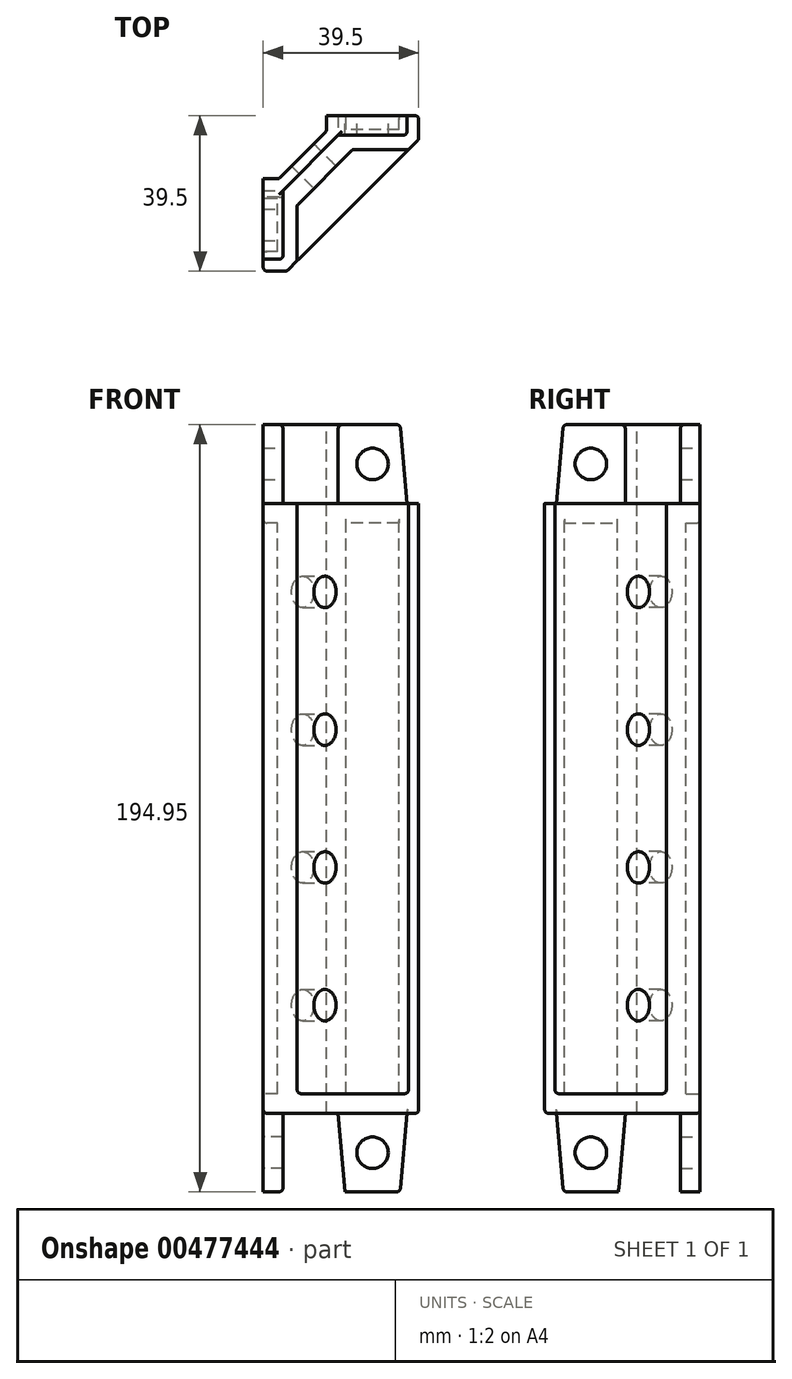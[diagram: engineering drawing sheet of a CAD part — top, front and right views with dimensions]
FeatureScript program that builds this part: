
annotation { "Feature Type Name" : "Feature", "Feature Type Description" : "" }
export const myFeature = defineFeature(function(context is Context, id is Id, definition is map)
    precondition{}
    {
        {
            var Q0;
            Q0=qCreatedBy(makeId("Top.planeOp"),FACE);
            var sketch = newSketch(context, id + "F0", { "sketchPlane" : qUnion([Q0])});
            skLineSegment(sketch, "E0", {"start": v(0, 30.13) * mm, "end": v(0, -27.95) * mm, "construction": true});
            skLineSegment(sketch, "E1", {"start": v(-25.65, 0) * mm, "end": v(27.57, 0) * mm, "construction": true});
            skLineSegment(sketch, "E2.bottom", {"start": v(-19.75, 19.75) * mm, "end": v(19.75, 19.75) * mm});
            skLineSegment(sketch, "E2.top", {"start": v(-19.75, -19.75) * mm, "end": v(-13.75, -19.75) * mm});
            skLineSegment(sketch, "E2.left", {"start": v(-19.75, 19.75) * mm, "end": v(-19.75, -19.75) * mm});
            skLineSegment(sketch, "E2.right", {"start": v(19.75, 19.75) * mm, "end": v(19.75, 13.75) * mm});
            skLineSegment(sketch, "E3", {"start": v(-13.75, -19.75) * mm, "end": v(19.75, 13.75) * mm});
            skSolve(sketch);
        }
        {
            var Q0;
            Q0 = qSketchRegion(id + "F0", true);
            extrude(context, id + "F1", {"entities" : qUnion([Q0]), "oppositeDirection" : true, "depth" : 155 * mm, "symmetric" : true});
        }
        {
            var Q0;
            Q0=makeQuery(id+"F1.opExtrude","CAP_FACE",FACE,{"disambiguationData":[OSD([sQuery(id+"F0.wireOp",EDGE,"E2.bottom"),sQuery(id+"F0.wireOp",EDGE,"E2.top"),sQuery(id+"F0.wireOp",EDGE,"E2.left"),sQuery(id+"F0.wireOp",EDGE,"E2.right"),sQuery(id+"F0.wireOp",EDGE,"E3")])],"isStart":true});
            var sketch = newSketch(context, id + "F2", { "sketchPlane" : qUnion([Q0])});
            skLineSegment(sketch, "E4", {"start": v(3, -3) * mm, "end": v(-19.75, 19.75) * mm, "construction": true});
            skLineSegment(sketch, "E5", {"start": v(3, -3) * mm, "end": v(17.14, 11.14) * mm});
            skLineSegment(sketch, "E6", {"start": v(3, -3) * mm, "end": v(-11.14, -17.14) * mm});
            skLineSegment(sketch, "E7", {"start": v(-11.14, -3) * mm, "end": v(3, 11.14) * mm});
            skLineSegment(sketch, "E8", {"start": v(-11.14, -17.14) * mm, "end": v(-11.14, -3) * mm});
            skLineSegment(sketch, "E9", {"start": v(3, 11.14) * mm, "end": v(17.14, 11.14) * mm});
            skSolve(sketch);
        }
        {
            var Q0;
            Q0 = qSketchRegion(id + "F2", true);
            extrude(context, id + "F3", {"entities" : qUnion([Q0]), "operationType" : NewBodyOperationType.REMOVE, "oppositeDirection" : true, "depth" : 150 * mm});
        }
        {
            var Q0;
            Q0=makeQuery(id+"F1.opExtrude","CAP_FACE",FACE,{"disambiguationData":[OSD([sQuery(id+"F0.wireOp",EDGE,"E2.bottom"),sQuery(id+"F0.wireOp",EDGE,"E2.top"),sQuery(id+"F0.wireOp",EDGE,"E2.left"),sQuery(id+"F0.wireOp",EDGE,"E2.right"),sQuery(id+"F0.wireOp",EDGE,"E3")])],"isStart":true});
            var sketch = newSketch(context, id + "F4", { "sketchPlane" : qUnion([Q0])});
            skPoint(sketch, "E10.orphan", {"position": v(-19.75, -19.75) * mm});
            skPoint(sketch, "E11.orphan", {"position": v(19.75, 19.75) * mm});
            skLineSegment(sketch, "E12", {"start": v(-19.75, 19.75) * mm, "end": v(-4.07, 4.07) * mm, "construction": true});
            skLineSegment(sketch, "E13", {"start": v(-15.75, 3.7) * mm, "end": v(-19.75, 3.7) * mm});
            skLineSegment(sketch, "E14", {"start": v(-3.7, 15.75) * mm, "end": v(-3.7, 19.75) * mm});
            skLineSegment(sketch, "E15", {"start": v(-3.7, 19.75) * mm, "end": v(-19.75, 19.75) * mm});
            skLineSegment(sketch, "E16", {"start": v(-19.75, 19.75) * mm, "end": v(-19.75, 3.7) * mm});
            skLineSegment(sketch, "E17", {"start": v(-3.7, 15.75) * mm, "end": v(-15.75, 3.7) * mm});
            skPoint(sketch, "E18.orphan", {"position": v(-14.68, 3.7) * mm});
            skPoint(sketch, "E19.orphan", {"position": v(-3.7, 13.6) * mm});
            skSolve(sketch);
        }
        {
            var Q0;
            Q0 = qSketchRegion(id + "F4", true);
            extrude(context, id + "F5", {"entities" : qUnion([Q0]), "operationType" : NewBodyOperationType.REMOVE, "endBound" : BoundingType.THROUGH_ALL, "oppositeDirection" : true, "depth" : 25 * mm});
        }
        {
            var Q0;
            Q0=makeQuery(id+"F1.opExtrude","CAP_FACE",FACE,{"disambiguationData":[OSD([sQuery(id+"F0.wireOp",EDGE,"E2.bottom"),sQuery(id+"F0.wireOp",EDGE,"E2.top"),sQuery(id+"F0.wireOp",EDGE,"E2.left"),sQuery(id+"F0.wireOp",EDGE,"E2.right"),sQuery(id+"F0.wireOp",EDGE,"E3")])],"isStart":true});
            var sketch = newSketch(context, id + "F6", { "sketchPlane" : qUnion([Q0])});
            skLineSegment(sketch, "E20.0", {"start": v(1.3, 16.14) * mm, "end": v(14.75, 16.14) * mm});
            skLineSegment(sketch, "E20.1", {"start": v(14.75, 19.75) * mm, "end": v(14.75, 16.14) * mm});
            skLineSegment(sketch, "E21.0", {"start": v(1.3, 16.14) * mm, "end": v(1.3, 19.75) * mm});
            skLineSegment(sketch, "E22", {"start": v(14.75, 19.75) * mm, "end": v(1.3, 19.75) * mm});
            skLineSegment(sketch, "E23.0", {"start": v(-16.14, -14.75) * mm, "end": v(-16.14, -1.3) * mm});
            skLineSegment(sketch, "E23.1", {"start": v(-19.75, -14.75) * mm, "end": v(-16.14, -14.75) * mm});
            skLineSegment(sketch, "E24.0", {"start": v(-16.14, -1.3) * mm, "end": v(-19.75, -1.3) * mm});
            skPoint(sketch, "E25.orphan", {"position": v(-12.53, -1.3) * mm});
            skLineSegment(sketch, "E26", {"start": v(-19.75, -14.75) * mm, "end": v(-19.75, -1.3) * mm});
            skSolve(sketch);
        }
        {
            var Q0;
            Q0 = qSketchRegion(id + "F6", true);
            extrude(context, id + "F7", {"entities" : qUnion([Q0]), "operationType" : NewBodyOperationType.REMOVE, "endBound" : BoundingType.THROUGH_ALL, "oppositeDirection" : true, "depth" : 25 * mm});
        }
        {
            var Q0;
            {var subQ1=sQuery(id+"F0.wireOp",EDGE,"E2.right");var subQ4=sQuery(id+"F0.wireOp",EDGE,"E2.bottom");Q0=makeQuery(id+"F7.boolean.opBoolean","SPLIT",FACE,{"disambiguationData":[TD([makeQuery(id+"F1.opExtrude","SWEPT_FACE",FACE,{"disambiguationData":[OSD([subQ1])]})])],"derivedFrom":makeQuery(id+"F1.opExtrude","SWEPT_FACE",FACE,{"disambiguationData":[OSD([subQ4])]})});}
            var sketch = newSketch(context, id + "F8", { "sketchPlane" : qUnion([Q0])});
            skLineSegment(sketch, "E27.bottom", {"start": v(-14.75, 77.5) * mm, "end": v(-1.3, 77.5) * mm});
            skLineSegment(sketch, "E27.top", {"start": v(-14.75, 72.5) * mm, "end": v(-1.3, 72.5) * mm});
            skLineSegment(sketch, "E27.left", {"start": v(-14.75, 77.5) * mm, "end": v(-14.75, 72.5) * mm});
            skLineSegment(sketch, "E27.right", {"start": v(-1.3, 77.5) * mm, "end": v(-1.3, 72.5) * mm});
            skLineSegment(sketch, "E28.bottom", {"start": v(-14.75, -77.5) * mm, "end": v(-1.3, -77.5) * mm});
            skLineSegment(sketch, "E28.top", {"start": v(-14.75, -72.5) * mm, "end": v(-1.3, -72.5) * mm});
            skLineSegment(sketch, "E28.left", {"start": v(-14.75, -77.5) * mm, "end": v(-14.75, -72.5) * mm});
            skLineSegment(sketch, "E28.right", {"start": v(-1.3, -77.5) * mm, "end": v(-1.3, -72.5) * mm});
            skSolve(sketch);
        }
        {
            var Q0;
            Q0 = qSketchRegion(id + "F8", true);
            var Q1;
            Q1=makeQuery(id+"F7.boolean.opBoolean","COPY",FACE,{"derivedFrom":makeQuery(id+"F7.opExtrude","SWEPT_FACE",FACE,{"disambiguationData":[OSD([sQuery(id+"F6.wireOp",EDGE,"E20.0")])]})});
            extrude(context, id + "F9", {"entities" : qUnion([Q0]), "operationType" : NewBodyOperationType.ADD, "endBound" : BoundingType.UP_TO_SURFACE, "oppositeDirection" : true, "endBoundEntityFace" : qUnion([Q1]), "depth" : 25 * mm});
        }
        {
            var Q0;
            {var subQ2=sQuery(id+"F0.wireOp",EDGE,"E2.left");var subQ3=sQuery(id+"F0.wireOp",EDGE,"E2.top");Q0=makeQuery(id+"F7.boolean.opBoolean","SPLIT",FACE,{"disambiguationData":[TD([makeQuery(id+"F1.opExtrude","SWEPT_FACE",FACE,{"disambiguationData":[OSD([subQ3])]})])],"derivedFrom":makeQuery(id+"F1.opExtrude","SWEPT_FACE",FACE,{"disambiguationData":[OSD([subQ2])]})});}
            var sketch = newSketch(context, id + "F10", { "sketchPlane" : qUnion([Q0])});
            skLineSegment(sketch, "E29.bottom", {"start": v(14.75, 77.5) * mm, "end": v(1.3, 77.5) * mm});
            skLineSegment(sketch, "E29.top", {"start": v(14.75, 72.5) * mm, "end": v(1.3, 72.5) * mm});
            skLineSegment(sketch, "E29.left", {"start": v(14.75, 77.5) * mm, "end": v(14.75, 72.5) * mm});
            skLineSegment(sketch, "E29.right", {"start": v(1.3, 77.5) * mm, "end": v(1.3, 72.5) * mm});
            skLineSegment(sketch, "E30.bottom", {"start": v(14.75, -77.5) * mm, "end": v(1.3, -77.5) * mm});
            skLineSegment(sketch, "E30.top", {"start": v(14.75, -72.5) * mm, "end": v(1.3, -72.5) * mm});
            skLineSegment(sketch, "E30.left", {"start": v(14.75, -77.5) * mm, "end": v(14.75, -72.5) * mm});
            skLineSegment(sketch, "E30.right", {"start": v(1.3, -77.5) * mm, "end": v(1.3, -72.5) * mm});
            skSolve(sketch);
        }
        {
            var Q0;
            Q0 = qSketchRegion(id + "F10", true);
            var Q1;
            Q1=makeQuery(id+"F7.boolean.opBoolean","COPY",FACE,{"derivedFrom":makeQuery(id+"F7.opExtrude","SWEPT_FACE",FACE,{"disambiguationData":[OSD([sQuery(id+"F6.wireOp",EDGE,"E23.0")])]})});
            extrude(context, id + "F11", {"entities" : qUnion([Q0]), "operationType" : NewBodyOperationType.ADD, "endBound" : BoundingType.UP_TO_SURFACE, "oppositeDirection" : true, "endBoundEntityFace" : qUnion([Q1]), "depth" : 25 * mm});
        }
        {
            var Q0;
            {var subQ2=sQuery(id+"F0.wireOp",EDGE,"E2.left");var subQ3=sQuery(id+"F0.wireOp",EDGE,"E2.top");var subQ7=makeQuery(id+"F1.opExtrude","SWEPT_FACE",FACE,{"disambiguationData":[OSD([subQ2])]});Q0=makeQuery(id+"F11.boolean.opBoolean","MERGE",FACE,{"derivedFrom":[makeQuery(id+"F7.boolean.opBoolean","SPLIT",FACE,{"disambiguationData":[TD([makeQuery(id+"F1.opExtrude","SWEPT_FACE",FACE,{"disambiguationData":[OSD([subQ3])]})])],"derivedFrom":subQ7}),makeQuery(id+"F7.boolean.opBoolean","SPLIT",FACE,{"disambiguationData":[TD([makeQuery(id+"F5.boolean.opBoolean","COPY",FACE,{"derivedFrom":makeQuery(id+"F5.opExtrude","SWEPT_FACE",FACE,{"disambiguationData":[OSD([sQuery(id+"F4.wireOp",EDGE,"E13")])]})})])],"derivedFrom":subQ7}),makeQuery(id+"F11.opExtrude","CAP_FACE",FACE,{"disambiguationData":[OSD([sQuery(id+"F10.wireOp",EDGE,"E29.bottom"),sQuery(id+"F10.wireOp",EDGE,"E29.top"),sQuery(id+"F10.wireOp",EDGE,"E29.left"),sQuery(id+"F10.wireOp",EDGE,"E29.right")])],"isStart":true}),makeQuery(id+"F11.opExtrude","CAP_FACE",FACE,{"disambiguationData":[OSD([sQuery(id+"F10.wireOp",EDGE,"E30.bottom"),sQuery(id+"F10.wireOp",EDGE,"E30.top"),sQuery(id+"F10.wireOp",EDGE,"E30.left"),sQuery(id+"F10.wireOp",EDGE,"E30.right")])],"isStart":true})]});}
            var sketch = newSketch(context, id + "F12", { "sketchPlane" : qUnion([Q0])});
            skLineSegment(sketch, "E31", {"start": v(8.02, 77.5) * mm, "end": v(8.02, 97.5) * mm, "construction": true});
            skLineSegment(sketch, "E32", {"start": v(0, 0) * mm, "end": v(35.4, 0) * mm, "construction": true});
            skPoint(sketch, "E32.endSnap0", {"position": v(19.75, 0) * mm});
            skLineSegment(sketch, "E33.MirrorCS", {"start": v(16.04, 0) * mm, "end": v(-19.35, 0) * mm, "construction": true});
            skLineSegment(sketch, "E34", {"start": v(16.75, 77.5) * mm, "end": v(-0.7, 77.5) * mm});
            skLineSegment(sketch, "E35", {"start": v(16.75, 77.5) * mm, "end": v(15.02, 97.5) * mm});
            skLineSegment(sketch, "E36", {"start": v(15.02, 97.5) * mm, "end": v(8.02, 97.5) * mm});
            skLineSegment(sketch, "E37", {"start": v(8.02, 97.5) * mm, "end": v(1.02, 97.5) * mm});
            skLineSegment(sketch, "E38", {"start": v(1.02, 97.5) * mm, "end": v(-0.7, 77.5) * mm});
            skLineSegment(sketch, "E39.MirrorCS", {"start": v(-0.7, 77.5) * mm, "end": v(1.02, 97.5) * mm});
            skSolve(sketch);
        }
        {
            var Q0;
            Q0 = qSketchRegion(id + "F12", true);
            extrude(context, id + "F13", {"entities" : qUnion([Q0]), "operationType" : NewBodyOperationType.ADD, "oppositeDirection" : true, "depth" : 5 * mm});
        }
        {
            var Q0;
            {var subQ1=sQuery(id+"F0.wireOp",EDGE,"E2.right");var subQ4=sQuery(id+"F0.wireOp",EDGE,"E2.bottom");var subQ7=makeQuery(id+"F1.opExtrude","SWEPT_FACE",FACE,{"disambiguationData":[OSD([subQ4])]});Q0=makeQuery(id+"F9.boolean.opBoolean","MERGE",FACE,{"derivedFrom":[makeQuery(id+"F7.boolean.opBoolean","SPLIT",FACE,{"disambiguationData":[TD([makeQuery(id+"F1.opExtrude","SWEPT_FACE",FACE,{"disambiguationData":[OSD([subQ1])]})])],"derivedFrom":subQ7}),makeQuery(id+"F7.boolean.opBoolean","SPLIT",FACE,{"disambiguationData":[TD([makeQuery(id+"F5.boolean.opBoolean","COPY",FACE,{"derivedFrom":makeQuery(id+"F5.opExtrude","SWEPT_FACE",FACE,{"disambiguationData":[OSD([sQuery(id+"F4.wireOp",EDGE,"E14")])]})})])],"derivedFrom":subQ7}),makeQuery(id+"F9.opExtrude","CAP_FACE",FACE,{"disambiguationData":[OSD([sQuery(id+"F8.wireOp",EDGE,"E27.bottom"),sQuery(id+"F8.wireOp",EDGE,"E27.top"),sQuery(id+"F8.wireOp",EDGE,"E27.left"),sQuery(id+"F8.wireOp",EDGE,"E27.right")])],"isStart":true}),makeQuery(id+"F9.opExtrude","CAP_FACE",FACE,{"disambiguationData":[OSD([sQuery(id+"F8.wireOp",EDGE,"E28.bottom"),sQuery(id+"F8.wireOp",EDGE,"E28.top"),sQuery(id+"F8.wireOp",EDGE,"E28.left"),sQuery(id+"F8.wireOp",EDGE,"E28.right")])],"isStart":true})]});}
            var sketch = newSketch(context, id + "F14", { "sketchPlane" : qUnion([Q0])});
            skLineSegment(sketch, "E40", {"start": v(-8.02, 77.5) * mm, "end": v(-8.02, 97.66) * mm, "construction": true});
            skPoint(sketch, "E40.endSnap0", {"position": v(-8.02, 77.5) * mm});
            skLineSegment(sketch, "E41", {"start": v(-15.02, 97.5) * mm, "end": v(-1.02, 97.5) * mm});
            skLineSegment(sketch, "E42", {"start": v(0, 0) * mm, "end": v(-60.6, 0) * mm, "construction": true});
            skPoint(sketch, "E42.endSnap0", {"position": v(-14.75, 0) * mm});
            skLineSegment(sketch, "E43", {"start": v(-15.02, 97.5) * mm, "end": v(-16.75, 77.5) * mm});
            skLineSegment(sketch, "E44", {"start": v(-1.02, 97.5) * mm, "end": v(0.7, 77.5) * mm});
            skLineSegment(sketch, "E45", {"start": v(0.7, 77.5) * mm, "end": v(-16.75, 77.5) * mm});
            skSolve(sketch);
        }
        {
            var Q0;
            Q0 = qSketchRegion(id + "F14", true);
            extrude(context, id + "F15", {"entities" : qUnion([Q0]), "operationType" : NewBodyOperationType.ADD, "oppositeDirection" : true, "depth" : 5 * mm});
        }
        {
            var Q0;
            {var subQ1=sQuery(id+"F0.wireOp",EDGE,"E2.right");var subQ4=sQuery(id+"F0.wireOp",EDGE,"E2.bottom");var subQ7=makeQuery(id+"F1.opExtrude","SWEPT_FACE",FACE,{"disambiguationData":[OSD([subQ4])]});Q0=makeQuery(id+"F15.boolean.opBoolean","MERGE",FACE,{"derivedFrom":[makeQuery(id+"F9.boolean.opBoolean","MERGE",FACE,{"derivedFrom":[makeQuery(id+"F7.boolean.opBoolean","SPLIT",FACE,{"disambiguationData":[TD([makeQuery(id+"F1.opExtrude","SWEPT_FACE",FACE,{"disambiguationData":[OSD([subQ1])]})])],"derivedFrom":subQ7}),makeQuery(id+"F7.boolean.opBoolean","SPLIT",FACE,{"disambiguationData":[TD([makeQuery(id+"F5.boolean.opBoolean","COPY",FACE,{"derivedFrom":makeQuery(id+"F5.opExtrude","SWEPT_FACE",FACE,{"disambiguationData":[OSD([sQuery(id+"F4.wireOp",EDGE,"E14")])]})})])],"derivedFrom":subQ7}),makeQuery(id+"F9.opExtrude","CAP_FACE",FACE,{"disambiguationData":[OSD([sQuery(id+"F8.wireOp",EDGE,"E27.bottom"),sQuery(id+"F8.wireOp",EDGE,"E27.top"),sQuery(id+"F8.wireOp",EDGE,"E27.left"),sQuery(id+"F8.wireOp",EDGE,"E27.right")])],"isStart":true}),makeQuery(id+"F9.opExtrude","CAP_FACE",FACE,{"disambiguationData":[OSD([sQuery(id+"F8.wireOp",EDGE,"E28.bottom"),sQuery(id+"F8.wireOp",EDGE,"E28.top"),sQuery(id+"F8.wireOp",EDGE,"E28.left"),sQuery(id+"F8.wireOp",EDGE,"E28.right")])],"isStart":true})]}),makeQuery(id+"F15.opExtrude","CAP_FACE",FACE,{"disambiguationData":[OSD([sQuery(id+"F14.wireOp",EDGE,"AjdLOBUI-PND2-HRux-vW9i-I60BuJFxOAxo"),sQuery(id+"F14.wireOp",EDGE,"m2E0O1S7-ugW4-w8lP-xUBK-8UGrL3XVD3p1"),sQuery(id+"F14.wireOp",EDGE,"E41"),sQuery(id+"F14.wireOp",EDGE,"z751VbyZ-Eswl-sp4i-D6d8-2ebrKqnJ25gN")])],"isStart":true}),makeQuery(id+"F15.opExtrude","CAP_FACE",FACE,{"disambiguationData":[OSD([sQuery(id+"F14.wireOp",EDGE,"9fced805-f766-4b14-a849-f1590210c0c81.MirrorCS"),sQuery(id+"F14.wireOp",EDGE,"9fced805-f766-4b14-a849-f1590210c0c82.MirrorCS"),sQuery(id+"F14.wireOp",EDGE,"9fced805-f766-4b14-a849-f1590210c0c83.MirrorCS"),sQuery(id+"F14.wireOp",EDGE,"9fced805-f766-4b14-a849-f1590210c0c84.MirrorCS")])],"isStart":true})]});}
            var sketch = newSketch(context, id + "F16", { "sketchPlane" : qUnion([Q0])});
            skLineSegment(sketch, "E46", {"start": v(-8.02, 97.5) * mm, "end": v(-8.02, -141.14) * mm, "construction": true});
            skCircle(sketch, "E47", {"center": v(-8.02, 87.5) * mm, "radius": 4 * mm});
            skSolve(sketch);
        }
        {
            var Q0;
            Q0 = qSketchRegion(id + "F16", true);
            extrude(context, id + "F17", {"entities" : qUnion([Q0]), "operationType" : NewBodyOperationType.REMOVE, "endBound" : BoundingType.THROUGH_ALL, "oppositeDirection" : true, "depth" : 25 * mm});
        }
        {
            var Q0;
            Q0=makeQuery(id+"F3.boolean.opBoolean","COPY",FACE,{"derivedFrom":makeQuery(id+"F3.opExtrude","SWEPT_FACE",FACE,{"disambiguationData":[OSD([sQuery(id+"F2.wireOp",EDGE,"E7")])]})});
            var sketch = newSketch(context, id + "F18", { "sketchPlane" : qUnion([Q0])});
            skLineSegment(sketch, "E48", {"start": v(0, 77.5) * mm, "end": v(0, -72.5) * mm, "construction": true});
            skLineSegment(sketch, "E49", {"start": v(0, 2.5) * mm, "end": v(10, 2.5) * mm, "construction": true});
            skCircle(sketch, "E50", {"center": v(0, 55) * mm, "radius": 4 * mm});
            skCircle(sketch, "E51", {"center": v(0, 20) * mm, "radius": 4 * mm});
            skCircle(sketch, "E52.MirrorC", {"center": v(0, -50) * mm, "radius": 4 * mm});
            skCircle(sketch, "E53.MirrorC", {"center": v(0, -15) * mm, "radius": 4 * mm});
            skSolve(sketch);
        }
        {
            var Q0;
            Q0 = qSketchRegion(id + "F18", true);
            extrude(context, id + "F19", {"entities" : qUnion([Q0]), "operationType" : NewBodyOperationType.REMOVE, "endBound" : BoundingType.THROUGH_ALL, "oppositeDirection" : true, "depth" : 25 * mm});
        }
        {
            var Q0;
            Q0=makeQuery(id+"F13.opExtrude","CAP_FACE",FACE,{"disambiguationData":[OSD([sQuery(id+"F12.wireOp",EDGE,"E34"),sQuery(id+"F12.wireOp",EDGE,"E35"),sQuery(id+"F12.wireOp",EDGE,"E36"),sQuery(id+"F12.wireOp",EDGE,"E37"),sQuery(id+"F12.wireOp",EDGE,"E39.MirrorCS")])],"isStart":false});
            var sketch = newSketch(context, id + "F20", { "sketchPlane" : qUnion([Q0])});
            skLineSegment(sketch, "E54", {"start": v(-8.02, 97.5) * mm, "end": v(-8.02, -97.5) * mm, "construction": true});
            skPoint(sketch, "E54.endSnap0", {"position": v(-8.02, 97.5) * mm});
            skCircle(sketch, "E55", {"center": v(-8.02, 87.5) * mm, "radius": 4 * mm});
            skSolve(sketch);
        }
        {
            var Q0;
            Q0 = qSketchRegion(id + "F20", true);
            extrude(context, id + "F21", {"entities" : qUnion([Q0]), "operationType" : NewBodyOperationType.REMOVE, "endBound" : BoundingType.THROUGH_ALL, "oppositeDirection" : true, "depth" : 25 * mm});
        }
        {
            var Q0;
            Q0=makeQuery(id+"F13.opExtrude","CAP_FACE",FACE,{"disambiguationData":[OSD([sQuery(id+"F12.wireOp",EDGE,"E34"),sQuery(id+"F12.wireOp",EDGE,"E35"),sQuery(id+"F12.wireOp",EDGE,"E36"),sQuery(id+"F12.wireOp",EDGE,"E37"),sQuery(id+"F12.wireOp",EDGE,"E39.MirrorCS")])],"isStart":false});
            var sketch = newSketch(context, id + "F22", { "sketchPlane" : qUnion([Q0])});
            skLineSegment(sketch, "E56", {"start": v(-16.75, -77.5) * mm, "end": v(-15.02, -97.5) * mm});
            skLineSegment(sketch, "E57", {"start": v(-15.02, -97.5) * mm, "end": v(-8.02, -97.5) * mm});
            skLineSegment(sketch, "E58", {"start": v(-8.02, -97.5) * mm, "end": v(-8.02, 83.5) * mm, "construction": true});
            skLineSegment(sketch, "E59.MirrorCS", {"start": v(0.7, -77.5) * mm, "end": v(-1.02, -97.5) * mm});
            skLineSegment(sketch, "E60.MirrorCS", {"start": v(-1.02, -97.5) * mm, "end": v(-8.02, -97.5) * mm});
            skLineSegment(sketch, "E61", {"start": v(-16.75, -77.5) * mm, "end": v(0.7, -77.5) * mm});
            skSolve(sketch);
        }
        {
            var Q0;
            Q0 = qSketchRegion(id + "F22", true);
            extrude(context, id + "F23", {"entities" : qUnion([Q0]), "operationType" : NewBodyOperationType.ADD, "oppositeDirection" : true, "depth" : 5 * mm});
        }
        {
            var Q0;
            Q0=makeQuery(id+"F15.opExtrude","CAP_FACE",FACE,{"disambiguationData":[OSD([sQuery(id+"F14.wireOp",EDGE,"E41"),sQuery(id+"F14.wireOp",EDGE,"E43"),sQuery(id+"F14.wireOp",EDGE,"E44"),sQuery(id+"F14.wireOp",EDGE,"E45")])],"isStart":false});
            var sketch = newSketch(context, id + "F24", { "sketchPlane" : qUnion([Q0])});
            skLineSegment(sketch, "E62", {"start": v(-0.7, -77.5) * mm, "end": v(1.02, -97.5) * mm});
            skLineSegment(sketch, "E63", {"start": v(1.02, -97.5) * mm, "end": v(8.02, -97.5) * mm});
            skLineSegment(sketch, "E64", {"start": v(8.02, -97.5) * mm, "end": v(8.02, -77.04) * mm, "construction": true});
            skLineSegment(sketch, "E65.MirrorCS", {"start": v(16.75, -77.5) * mm, "end": v(15.02, -97.5) * mm});
            skLineSegment(sketch, "E66.MirrorCS", {"start": v(15.02, -97.5) * mm, "end": v(8.02, -97.5) * mm});
            skLineSegment(sketch, "E67", {"start": v(-0.7, -77.5) * mm, "end": v(16.75, -77.5) * mm});
            skSolve(sketch);
        }
        {
            var Q0;
            Q0 = qSketchRegion(id + "F24", true);
            extrude(context, id + "F25", {"entities" : qUnion([Q0]), "operationType" : NewBodyOperationType.ADD, "oppositeDirection" : true, "depth" : 5 * mm});
        }
        {
            var Q0;
            Q0=makeQuery(id+"F23.opExtrude","CAP_FACE",FACE,{"disambiguationData":[OSD([sQuery(id+"F22.wireOp",EDGE,"E56"),sQuery(id+"F22.wireOp",EDGE,"E57"),sQuery(id+"F22.wireOp",EDGE,"E59.MirrorCS"),sQuery(id+"F22.wireOp",EDGE,"E60.MirrorCS"),sQuery(id+"F22.wireOp",EDGE,"E61")])],"isStart":false});
            var sketch = newSketch(context, id + "F26", { "sketchPlane" : qUnion([Q0])});
            skLineSegment(sketch, "E68", {"start": v(8.02, -97.5) * mm, "end": v(8.02, -77.5) * mm, "construction": true});
            skCircle(sketch, "E69", {"center": v(8.02, -87.5) * mm, "radius": 4 * mm});
            skSolve(sketch);
        }
        {
            var Q0;
            Q0 = qSketchRegion(id + "F26", true);
            extrude(context, id + "F27", {"entities" : qUnion([Q0]), "operationType" : NewBodyOperationType.REMOVE, "oppositeDirection" : true, "depth" : 25 * mm});
        }
        {
            var Q0;
            Q0=makeQuery(id+"F25.opExtrude","CAP_FACE",FACE,{"disambiguationData":[OSD([sQuery(id+"F24.wireOp",EDGE,"E62"),sQuery(id+"F24.wireOp",EDGE,"E63"),sQuery(id+"F24.wireOp",EDGE,"E65.MirrorCS"),sQuery(id+"F24.wireOp",EDGE,"E66.MirrorCS"),sQuery(id+"F24.wireOp",EDGE,"E67")])],"isStart":false});
            var sketch = newSketch(context, id + "F28", { "sketchPlane" : qUnion([Q0])});
            skLineSegment(sketch, "E70", {"start": v(-8.02, -97.5) * mm, "end": v(-8.02, -77.5) * mm, "construction": true});
            skCircle(sketch, "E71", {"center": v(-8.02, -87.5) * mm, "radius": 4 * mm});
            skSolve(sketch);
        }
        {
            var Q0;
            Q0 = qSketchRegion(id + "F28", true);
            extrude(context, id + "F29", {"entities" : qUnion([Q0]), "operationType" : NewBodyOperationType.REMOVE, "oppositeDirection" : true, "depth" : 25 * mm});
        }
        {
            var Q0;
            Q0=makeQuery(id+"F11.boolean.opBoolean","MERGE",FACE,{"derivedFrom":[makeQuery(id+"F9.boolean.opBoolean","MERGE",FACE,{"derivedFrom":[makeQuery(id+"F1.opExtrude","CAP_FACE",FACE,{"disambiguationData":[OSD([sQuery(id+"F0.wireOp",EDGE,"E2.bottom"),sQuery(id+"F0.wireOp",EDGE,"E2.top"),sQuery(id+"F0.wireOp",EDGE,"E2.left"),sQuery(id+"F0.wireOp",EDGE,"E2.right"),sQuery(id+"F0.wireOp",EDGE,"E3")])],"isStart":true}),makeQuery(id+"F9.opExtrude","SWEPT_FACE",FACE,{"disambiguationData":[OSD([sQuery(id+"F8.wireOp",EDGE,"E27.bottom")])]})]}),makeQuery(id+"F11.opExtrude","SWEPT_FACE",FACE,{"disambiguationData":[OSD([sQuery(id+"F10.wireOp",EDGE,"E29.bottom")])]})]});
            var sketch = newSketch(context, id + "F30", { "sketchPlane" : qUnion([Q0])});
            skLineSegment(sketch, "E72.0", {"start": v(-19.75, 0.7) * mm, "end": v(-19.75, -1.02) * mm});
            skLineSegment(sketch, "E72.1", {"start": v(-19.75, 3.7) * mm, "end": v(-19.75, 0.7) * mm});
            skLineSegment(sketch, "E72.2", {"start": v(-15.75, 3.7) * mm, "end": v(-19.75, 3.7) * mm});
            skLineSegment(sketch, "E72.3", {"start": v(-3.7, 15.75) * mm, "end": v(-15.75, 3.7) * mm});
            skLineSegment(sketch, "E72.4", {"start": v(-3.7, 15.75) * mm, "end": v(-3.7, 19.75) * mm});
            skLineSegment(sketch, "E72.5", {"start": v(-3.7, 19.75) * mm, "end": v(-0.7, 19.75) * mm});
            skLineSegment(sketch, "E72.6", {"start": v(1.02, 19.75) * mm, "end": v(-0.7, 19.75) * mm});
            skLineSegment(sketch, "E72.7", {"start": v(1.02, 14.75) * mm, "end": v(1.02, 19.75) * mm});
            skLineSegment(sketch, "E72.8", {"start": v(-14.75, -1.02) * mm, "end": v(-19.75, -1.02) * mm});
            skLineSegment(sketch, "E73", {"start": v(-14.75, -1.02) * mm, "end": v(-14.75, 0.7) * mm});
            skLineSegment(sketch, "E74", {"start": v(1.02, 14.75) * mm, "end": v(-0.7, 14.75) * mm});
            skLineSegment(sketch, "E75", {"start": v(-0.7, 14.75) * mm, "end": v(-14.75, 0.7) * mm});
            skSolve(sketch);
        }
        {
            var Q0;
            Q0 = qSketchRegion(id + "F30", true);
            extrude(context, id + "F31", {"entities" : qUnion([Q0]), "operationType" : NewBodyOperationType.ADD, "depth" : 20 * mm});
        }
        {
            var Q0;
            {var subQ0=sQuery(id+"F30.wireOp",EDGE,"E72.6");var subQ1=sQuery(id+"F30.wireOp",EDGE,"E72.5");var subQ3=sQuery(id+"F0.wireOp",EDGE,"E2.right");var subQ6=sQuery(id+"F0.wireOp",EDGE,"E2.bottom");var subQ9=makeQuery(id+"F1.opExtrude","SWEPT_FACE",FACE,{"disambiguationData":[OSD([subQ6])]});Q0=makeQuery(id+"FBWLq7zkuCnlSsx_1.1.F31.boolean.opBoolean","MERGE",FACE,{"derivedFrom":[makeQuery(id+"F31.boolean.opBoolean","MERGE",FACE,{"derivedFrom":[makeQuery(id+"F25.boolean.opBoolean","MERGE",FACE,{"derivedFrom":[makeQuery(id+"F15.boolean.opBoolean","MERGE",FACE,{"derivedFrom":[makeQuery(id+"F9.boolean.opBoolean","MERGE",FACE,{"derivedFrom":[makeQuery(id+"F7.boolean.opBoolean","SPLIT",FACE,{"disambiguationData":[TD([makeQuery(id+"F1.opExtrude","SWEPT_FACE",FACE,{"disambiguationData":[OSD([subQ3])]})])],"derivedFrom":subQ9}),makeQuery(id+"F7.boolean.opBoolean","SPLIT",FACE,{"disambiguationData":[TD([makeQuery(id+"F5.boolean.opBoolean","COPY",FACE,{"derivedFrom":makeQuery(id+"F5.opExtrude","SWEPT_FACE",FACE,{"disambiguationData":[OSD([sQuery(id+"F4.wireOp",EDGE,"E14")])]})})])],"derivedFrom":subQ9}),makeQuery(id+"F9.opExtrude","CAP_FACE",FACE,{"disambiguationData":[OSD([sQuery(id+"F8.wireOp",EDGE,"E27.bottom"),sQuery(id+"F8.wireOp",EDGE,"E27.top"),sQuery(id+"F8.wireOp",EDGE,"E27.left"),sQuery(id+"F8.wireOp",EDGE,"E27.right")])],"isStart":true}),makeQuery(id+"F9.opExtrude","CAP_FACE",FACE,{"disambiguationData":[OSD([sQuery(id+"F8.wireOp",EDGE,"E28.bottom"),sQuery(id+"F8.wireOp",EDGE,"E28.top"),sQuery(id+"F8.wireOp",EDGE,"E28.left"),sQuery(id+"F8.wireOp",EDGE,"E28.right")])],"isStart":true})]}),makeQuery(id+"F15.opExtrude","CAP_FACE",FACE,{"disambiguationData":[OSD([sQuery(id+"F14.wireOp",EDGE,"E41"),sQuery(id+"F14.wireOp",EDGE,"E43"),sQuery(id+"F14.wireOp",EDGE,"E44"),sQuery(id+"F14.wireOp",EDGE,"E45")])],"isStart":true})]}),makeQuery(id+"F25.opExtrude","CAP_FACE",FACE,{"disambiguationData":[OSD([sQuery(id+"F24.wireOp",EDGE,"E62"),sQuery(id+"F24.wireOp",EDGE,"E63"),sQuery(id+"F24.wireOp",EDGE,"E65.MirrorCS"),sQuery(id+"F24.wireOp",EDGE,"E66.MirrorCS"),sQuery(id+"F24.wireOp",EDGE,"E67")])],"isStart":false})]}),makeQuery(id+"F31.opExtrude","SWEPT_FACE",FACE,{"disambiguationData":[OSD([subQ1,subQ0])]})]}),makeQuery(id+"FBWLq7zkuCnlSsx_1.1.F31.opExtrude","SWEPT_FACE",FACE,{"disambiguationData":[OSD([subQ1,subQ0])]})]});}
            var sketch = newSketch(context, id + "F32", { "sketchPlane" : qUnion([Q0])});
            skLineSegment(sketch, "E76.bottom", {"start": v(26.29, -110.54) * mm, "end": v(-19.54, -110.54) * mm});
            skLineSegment(sketch, "E76.top", {"start": v(26.29, -97.45) * mm, "end": v(-19.54, -97.45) * mm});
            skLineSegment(sketch, "E76.left", {"start": v(26.29, -110.54) * mm, "end": v(26.29, -97.45) * mm});
            skLineSegment(sketch, "E76.right", {"start": v(-19.54, -110.54) * mm, "end": v(-19.54, -97.45) * mm});
            skSolve(sketch);
        }
        {
            var Q0;
            Q0 = qSketchRegion(id + "F32", true);
            extrude(context, id + "F33", {"entities" : qUnion([Q0]), "operationType" : NewBodyOperationType.REMOVE, "oppositeDirection" : true, "depth" : 100 * mm, "symmetric" : true});
        }
        {
            var Q0;
            Q0=makeQuery(id+"F13.opExtrude","SWEPT_EDGE",EDGE,{"disambiguationData":[OSD([sQuery(id+"F12.wireOp",EDGE,"E35"),sQuery(id+"F12.wireOp",EDGE,"E36")])]});
            var Q1;
            Q1=makeQuery(id+"F13.opExtrude","SWEPT_EDGE",EDGE,{"disambiguationData":[OSD([sQuery(id+"F12.wireOp",EDGE,"E37"),sQuery(id+"F12.wireOp",EDGE,"E39.MirrorCS")])]});
            var Q2;
            Q2=makeQuery(id+"F15.opExtrude","SWEPT_EDGE",EDGE,{"disambiguationData":[OSD([sQuery(id+"F14.wireOp",EDGE,"E41"),sQuery(id+"F14.wireOp",EDGE,"E43")])]});
            var Q3;
            Q3=makeQuery(id+"F15.opExtrude","SWEPT_EDGE",EDGE,{"disambiguationData":[OSD([sQuery(id+"F14.wireOp",EDGE,"E41"),sQuery(id+"F14.wireOp",EDGE,"E44")])]});
            var Q4;
            Q4=makeQuery(id+"F15.opExtrude","SWEPT_EDGE",EDGE,{"disambiguationData":[OSD([sQuery(id+"F14.wireOp",EDGE,"14d68a54-c34f-48c8-ae77-41faf57796821.MirrorCS"),sQuery(id+"F14.wireOp",EDGE,"14d68a54-c34f-48c8-ae77-41faf57796823.MirrorCS")])]});
            var Q5;
            Q5=makeQuery(id+"F15.opExtrude","SWEPT_EDGE",EDGE,{"disambiguationData":[OSD([sQuery(id+"F14.wireOp",EDGE,"14d68a54-c34f-48c8-ae77-41faf57796820.MirrorCS"),sQuery(id+"F14.wireOp",EDGE,"14d68a54-c34f-48c8-ae77-41faf57796823.MirrorCS")])]});
            var Q6;
            Q6=makeQuery(id+"F13.opExtrude","SWEPT_EDGE",EDGE,{"disambiguationData":[OSD([sQuery(id+"F12.wireOp",EDGE,"0e25475b-3a4a-4502-b2ef-1a4ccfbb12351.MirrorCS"),sQuery(id+"F12.wireOp",EDGE,"0e25475b-3a4a-4502-b2ef-1a4ccfbb12353.MirrorCS")])]});
            var Q7;
            Q7=makeQuery(id+"F13.opExtrude","SWEPT_EDGE",EDGE,{"disambiguationData":[OSD([sQuery(id+"F12.wireOp",EDGE,"0e25475b-3a4a-4502-b2ef-1a4ccfbb12352.MirrorCS"),sQuery(id+"F12.wireOp",EDGE,"0e25475b-3a4a-4502-b2ef-1a4ccfbb12353.MirrorCS")])]});
            var Q8;
            Q8=makeQuery(id+"F1.opExtrude","SWEPT_EDGE",EDGE,{"disambiguationData":[OSD([sQuery(id+"F0.wireOp",EDGE,"E2.top"),sQuery(id+"F0.wireOp",EDGE,"E3")])]});
            var Q9;
            Q9=makeQuery(id+"F1.opExtrude","SWEPT_EDGE",EDGE,{"disambiguationData":[OSD([sQuery(id+"F0.wireOp",EDGE,"E2.right"),sQuery(id+"F0.wireOp",EDGE,"E3")])]});
            var Q10;
            Q10=makeQuery(id+"F3.boolean.opBoolean","COPY",EDGE,{"derivedFrom":makeQuery(id+"F3.opExtrude","SWEPT_EDGE",EDGE,{"disambiguationData":[OSD([sQuery(id+"F2.wireOp",EDGE,"E7"),sQuery(id+"F2.wireOp",EDGE,"E8")])]})});
            var Q11;
            Q11=makeQuery(id+"F3.boolean.opBoolean","COPY",EDGE,{"derivedFrom":makeQuery(id+"F3.opExtrude","SWEPT_EDGE",EDGE,{"disambiguationData":[OSD([sQuery(id+"F2.wireOp",EDGE,"E7"),sQuery(id+"F2.wireOp",EDGE,"E9")])]})});
            var Q12;
            Q12=makeQuery(id+"F5.boolean.opBoolean","COPY",EDGE,{"derivedFrom":makeQuery(id+"F5.opExtrude","SWEPT_EDGE",EDGE,{"disambiguationData":[OSD([sQuery(id+"F4.wireOp",EDGE,"E13"),sQuery(id+"F4.wireOp",EDGE,"E17")])]})});
            var Q13;
            Q13=makeQuery(id+"F5.boolean.opBoolean","COPY",EDGE,{"derivedFrom":makeQuery(id+"F5.opExtrude","SWEPT_EDGE",EDGE,{"disambiguationData":[OSD([sQuery(id+"F4.wireOp",EDGE,"E14"),sQuery(id+"F4.wireOp",EDGE,"E17")])]})});
            var Q14;
            Q14=makeQuery(id+"F5.boolean.opBoolean","COPY",EDGE,{"derivedFrom":makeQuery(id+"F5.opExtrude","SWEPT_EDGE",EDGE,{"disambiguationData":[OSD([sQuery(id+"F0.wireOp",EDGE,"E2.bottom"),sQuery(id+"F4.wireOp",EDGE,"E14"),sQuery(id+"F4.wireOp",EDGE,"E15")])]})});
            var Q15;
            Q15=makeQuery(id+"F5.boolean.opBoolean","COPY",EDGE,{"derivedFrom":makeQuery(id+"F5.opExtrude","SWEPT_EDGE",EDGE,{"disambiguationData":[OSD([sQuery(id+"F0.wireOp",EDGE,"E2.left"),sQuery(id+"F4.wireOp",EDGE,"E13"),sQuery(id+"F4.wireOp",EDGE,"E16")])]})});
            var Q16;
            Q16=makeQuery(id+"F11.opExtrude","SWEPT_EDGE",EDGE,{"disambiguationData":[OSD([sQuery(id+"F0.wireOp",EDGE,"E2.left"),sQuery(id+"F6.wireOp",EDGE,"E23.1"),sQuery(id+"F6.wireOp",EDGE,"E26"),sQuery(id+"F10.wireOp",EDGE,"E29.top"),sQuery(id+"F10.wireOp",EDGE,"E29.left")])]});
            var Q17;
            Q17=makeQuery(id+"F11.opExtrude","SWEPT_EDGE",EDGE,{"disambiguationData":[OSD([sQuery(id+"F10.wireOp",EDGE,"E29.top"),sQuery(id+"F10.wireOp",EDGE,"E29.right")])]});
            var Q18;
            Q18=makeQuery(id+"F11.opExtrude","SWEPT_EDGE",EDGE,{"disambiguationData":[OSD([sQuery(id+"F10.wireOp",EDGE,"E30.top"),sQuery(id+"F10.wireOp",EDGE,"E30.right")])]});
            var Q19;
            Q19=makeQuery(id+"F11.opExtrude","SWEPT_EDGE",EDGE,{"disambiguationData":[OSD([sQuery(id+"F0.wireOp",EDGE,"E2.left"),sQuery(id+"F6.wireOp",EDGE,"E23.1"),sQuery(id+"F6.wireOp",EDGE,"E26"),sQuery(id+"F10.wireOp",EDGE,"E30.top"),sQuery(id+"F10.wireOp",EDGE,"E30.left")])]});
            var Q20;
            Q20=makeQuery(id+"F9.opExtrude","SWEPT_EDGE",EDGE,{"disambiguationData":[OSD([sQuery(id+"F0.wireOp",EDGE,"E2.bottom"),sQuery(id+"F6.wireOp",EDGE,"E20.1"),sQuery(id+"F6.wireOp",EDGE,"E22"),sQuery(id+"F8.wireOp",EDGE,"E28.top"),sQuery(id+"F8.wireOp",EDGE,"E28.left")])]});
            var Q21;
            Q21=makeQuery(id+"F9.opExtrude","SWEPT_EDGE",EDGE,{"disambiguationData":[OSD([sQuery(id+"F8.wireOp",EDGE,"E28.top"),sQuery(id+"F8.wireOp",EDGE,"E28.right")])]});
            var Q22;
            Q22=makeQuery(id+"F9.opExtrude","SWEPT_EDGE",EDGE,{"disambiguationData":[OSD([sQuery(id+"F0.wireOp",EDGE,"E2.bottom"),sQuery(id+"F6.wireOp",EDGE,"E20.1"),sQuery(id+"F6.wireOp",EDGE,"E22"),sQuery(id+"F8.wireOp",EDGE,"E27.top"),sQuery(id+"F8.wireOp",EDGE,"E27.left")])]});
            var Q23;
            Q23=makeQuery(id+"F9.opExtrude","SWEPT_EDGE",EDGE,{"disambiguationData":[OSD([sQuery(id+"F8.wireOp",EDGE,"E27.top"),sQuery(id+"F8.wireOp",EDGE,"E27.right")])]});
            var Q24;
            Q24=makeQuery(id+"F33.boolean.opBoolean","INTERSECT",EDGE,{"derivedFrom":[makeQuery(id+"F23.opExtrude","SWEPT_FACE",FACE,{"disambiguationData":[OSD([sQuery(id+"F22.wireOp",EDGE,"E56")])]}),makeQuery(id+"F33.opExtrude","SWEPT_FACE",FACE,{"disambiguationData":[OSD([sQuery(id+"F32.wireOp",EDGE,"E76.top")])]})]});
            var Q25;
            Q25=makeQuery(id+"F33.boolean.opBoolean","INTERSECT",EDGE,{"derivedFrom":[makeQuery(id+"F25.opExtrude","SWEPT_FACE",FACE,{"disambiguationData":[OSD([sQuery(id+"F24.wireOp",EDGE,"E65.MirrorCS")])]}),makeQuery(id+"F33.opExtrude","SWEPT_FACE",FACE,{"disambiguationData":[OSD([sQuery(id+"F32.wireOp",EDGE,"E76.top")])]})]});
            var Q26;
            Q26=makeQuery(id+"FBWLq7zkuCnlSsx_1.1.F31.opExtrude","SWEPT_EDGE",EDGE,{"disambiguationData":[OSD([sQuery(id+"F0.wireOp",EDGE,"E2.left"),sQuery(id+"F10.wireOp",EDGE,"E29.bottom"),sQuery(id+"F12.wireOp",EDGE,"E34"),sQuery(id+"F12.wireOp",EDGE,"E39.MirrorCS"),sQuery(id+"F30.wireOp",EDGE,"E73"),sQuery(id+"F30.wireOp",EDGE,"TVdcdLyP-e3im-owOH-fyVM-Xv4wgL9olcjO")])]});
            var Q27;
            Q27=makeQuery(id+"FBWLq7zkuCnlSsx_1.1.F31.opExtrude","SWEPT_EDGE",EDGE,{"disambiguationData":[OSD([sQuery(id+"F0.wireOp",EDGE,"E2.bottom"),sQuery(id+"F8.wireOp",EDGE,"E27.bottom"),sQuery(id+"F14.wireOp",EDGE,"E44"),sQuery(id+"F14.wireOp",EDGE,"E45"),sQuery(id+"F30.wireOp",EDGE,"E74"),sQuery(id+"F30.wireOp",EDGE,"Y2WSOVF7-zBNb-A4NI-rEHm-fRtvpLz0GWT2")])]});
            var Q28;
            Q28=makeQuery(id+"F31.opExtrude","SWEPT_EDGE",EDGE,{"disambiguationData":[OSD([sQuery(id+"F0.wireOp",EDGE,"E2.left"),sQuery(id+"F10.wireOp",EDGE,"E29.bottom"),sQuery(id+"F12.wireOp",EDGE,"E34"),sQuery(id+"F12.wireOp",EDGE,"E39.MirrorCS"),sQuery(id+"F30.wireOp",EDGE,"E73"),sQuery(id+"F30.wireOp",EDGE,"TVdcdLyP-e3im-owOH-fyVM-Xv4wgL9olcjO")])]});
            var Q29;
            Q29=makeQuery(id+"F31.opExtrude","SWEPT_EDGE",EDGE,{"disambiguationData":[OSD([sQuery(id+"F0.wireOp",EDGE,"E2.bottom"),sQuery(id+"F8.wireOp",EDGE,"E27.bottom"),sQuery(id+"F14.wireOp",EDGE,"E44"),sQuery(id+"F14.wireOp",EDGE,"E45"),sQuery(id+"F30.wireOp",EDGE,"E74"),sQuery(id+"F30.wireOp",EDGE,"Y2WSOVF7-zBNb-A4NI-rEHm-fRtvpLz0GWT2")])]});
            fillet(context, id + "F34", {"entities" : qUnion([Q0, Q1, Q2, Q3, Q4, Q5, Q6, Q7, Q8, Q9, Q10, Q11, Q12, Q13, Q14, Q15, Q16, Q17, Q18, Q19, Q20, Q21, Q22, Q23, Q24, Q25, Q26, Q27, Q28, Q29]), "radius" : 1 * mm, "tangentPropagation" : true, "allowEdgeOverflow" : false});
        }
        {
            var Q0;
            Q0=makeQuery(id+"F3.boolean.opBoolean","COPY",EDGE,{"derivedFrom":makeQuery(id+"F3.opExtrude","CAP_EDGE",EDGE,{"disambiguationData":[OSD([sQuery(id+"F2.wireOp",EDGE,"E8")])],"isStart":false})});
            var Q1;
            Q1=makeQuery(id+"F15.opExtrude","CAP_EDGE",EDGE,{"disambiguationData":[OSD([sQuery(id+"F14.wireOp",EDGE,"14d68a54-c34f-48c8-ae77-41faf57796821.MirrorCS")])],"isStart":false});
            var Q2;
            Q2=makeQuery(id+"F13.opExtrude","CAP_EDGE",EDGE,{"disambiguationData":[OSD([sQuery(id+"F12.wireOp",EDGE,"0e25475b-3a4a-4502-b2ef-1a4ccfbb12352.MirrorCS")])],"isStart":false});
            var Q3;
            Q3=makeQuery(id+"F13.opExtrude","CAP_EDGE",EDGE,{"disambiguationData":[OSD([sQuery(id+"F12.wireOp",EDGE,"E35")])],"isStart":false});
            var Q4;
            Q4=makeQuery(id+"F15.opExtrude","CAP_EDGE",EDGE,{"disambiguationData":[OSD([sQuery(id+"F14.wireOp",EDGE,"E43")])],"isStart":false});
            var Q5;
            Q5=makeQuery(id+"F9.opExtrude","TWEAK_EDGE",EDGE,{"derivedFrom":[makeQuery(id+"F7.boolean.opBoolean","COPY",FACE,{"derivedFrom":makeQuery(id+"F7.opExtrude","SWEPT_FACE",FACE,{"disambiguationData":[OSD([sQuery(id+"F6.wireOp",EDGE,"E20.0")])]})}),makeQuery(id+"F8.imprint","IMPRINT",EDGE,{"derivedFrom":sQuery(id+"F8.wireOp",EDGE,"E27.top")})]});
            var Q6;
            Q6=makeQuery(id+"F9.opExtrude","CAP_EDGE",EDGE,{"disambiguationData":[OSD([sQuery(id+"F8.wireOp",EDGE,"E27.top")])],"isStart":true});
            var Q7;
            Q7=makeQuery(id+"F11.opExtrude","TWEAK_EDGE",EDGE,{"derivedFrom":[makeQuery(id+"F7.boolean.opBoolean","COPY",FACE,{"derivedFrom":makeQuery(id+"F7.opExtrude","SWEPT_FACE",FACE,{"disambiguationData":[OSD([sQuery(id+"F6.wireOp",EDGE,"E23.0")])]})}),makeQuery(id+"F10.imprint","IMPRINT",EDGE,{"derivedFrom":sQuery(id+"F10.wireOp",EDGE,"E29.top")})]});
            var Q8;
            Q8=makeQuery(id+"F11.opExtrude","CAP_EDGE",EDGE,{"disambiguationData":[OSD([sQuery(id+"F10.wireOp",EDGE,"E29.top")])],"isStart":true});
            var Q9;
            Q9=makeQuery(id+"F23.opExtrude","SWEPT_EDGE",EDGE,{"disambiguationData":[OSD([sQuery(id+"F22.wireOp",EDGE,"E56"),sQuery(id+"F22.wireOp",EDGE,"E57")])]});
            var Q10;
            Q10=makeQuery(id+"F23.opExtrude","SWEPT_EDGE",EDGE,{"disambiguationData":[OSD([sQuery(id+"F22.wireOp",EDGE,"E59.MirrorCS"),sQuery(id+"F22.wireOp",EDGE,"E60.MirrorCS")])]});
            var Q11;
            Q11=makeQuery(id+"F25.opExtrude","SWEPT_EDGE",EDGE,{"disambiguationData":[OSD([sQuery(id+"F24.wireOp",EDGE,"E62"),sQuery(id+"F24.wireOp",EDGE,"E63")])]});
            var Q12;
            Q12=makeQuery(id+"F25.opExtrude","SWEPT_EDGE",EDGE,{"disambiguationData":[OSD([sQuery(id+"F24.wireOp",EDGE,"E65.MirrorCS"),sQuery(id+"F24.wireOp",EDGE,"E66.MirrorCS")])]});
            var Q13;
            Q13=makeQuery(id+"F23.opExtrude","CAP_EDGE",EDGE,{"disambiguationData":[OSD([sQuery(id+"F22.wireOp",EDGE,"E56")])],"isStart":true});
            fillet(context, id + "F35", {"entities" : qUnion([Q0, Q1, Q2, Q3, Q4, Q5, Q6, Q7, Q8, Q9, Q10, Q11, Q12, Q13]), "radius" : 1 * mm, "tangentPropagation" : true, "allowEdgeOverflow" : false});
        }
        {
            var Q0;
            Q0=makeQuery(id+"F3.boolean.opBoolean","COPY",EDGE,{"derivedFrom":makeQuery(id+"F3.opExtrude","SWEPT_EDGE",EDGE,{"disambiguationData":[OSD([sQuery(id+"F0.wireOp",EDGE,"E3"),sQuery(id+"F2.wireOp",EDGE,"E6"),sQuery(id+"F2.wireOp",EDGE,"E8")])]})});
            var Q1;
            Q1=makeQuery(id+"F13.opExtrude","SWEPT_EDGE",EDGE,{"disambiguationData":[OSD([sQuery(id+"F0.wireOp",EDGE,"E2.left"),sQuery(id+"F10.wireOp",EDGE,"E29.bottom"),sQuery(id+"F12.wireOp",EDGE,"E34"),sQuery(id+"F12.wireOp",EDGE,"E35")])]});
            var Q2;
            Q2=makeQuery(id+"F15.opExtrude","SWEPT_EDGE",EDGE,{"disambiguationData":[OSD([sQuery(id+"F0.wireOp",EDGE,"E2.bottom"),sQuery(id+"F8.wireOp",EDGE,"E27.bottom"),sQuery(id+"F14.wireOp",EDGE,"E43"),sQuery(id+"F14.wireOp",EDGE,"E45")])]});
            var Q3;
            Q3=makeQuery(id+"F13.opExtrude","SWEPT_EDGE",EDGE,{"disambiguationData":[OSD([sQuery(id+"F0.wireOp",EDGE,"E2.left"),sQuery(id+"F10.wireOp",EDGE,"E30.bottom"),sQuery(id+"F12.wireOp",EDGE,"0e25475b-3a4a-4502-b2ef-1a4ccfbb12352.MirrorCS"),sQuery(id+"F12.wireOp",EDGE,"0e25475b-3a4a-4502-b2ef-1a4ccfbb12354.MirrorCS")])]});
            var Q4;
            Q4=makeQuery(id+"F15.opExtrude","CAP_EDGE",EDGE,{"disambiguationData":[OSD([sQuery(id+"F14.wireOp",EDGE,"14d68a54-c34f-48c8-ae77-41faf57796822.MirrorCS")])],"isStart":false});
            var Q5;
            Q5=makeQuery(id+"F1.opExtrude","SWEPT_EDGE",EDGE,{"disambiguationData":[OSD([sQuery(id+"F0.wireOp",EDGE,"E2.bottom"),sQuery(id+"F0.wireOp",EDGE,"E2.right")])]});
            var Q6;
            Q6=makeQuery(id+"F1.opExtrude","SWEPT_EDGE",EDGE,{"disambiguationData":[OSD([sQuery(id+"F0.wireOp",EDGE,"E2.top"),sQuery(id+"F0.wireOp",EDGE,"E2.left")])]});
            var Q7;
            Q7=makeQuery(id+"F23.opExtrude","CAP_EDGE",EDGE,{"disambiguationData":[OSD([sQuery(id+"F22.wireOp",EDGE,"E61")])],"isStart":true});
            fillet(context, id + "F36", {"entities" : qUnion([Q0, Q1, Q2, Q3, Q4, Q5, Q6, Q7]), "radius" : 1 * mm, "tangentPropagation" : true, "allowEdgeOverflow" : false});
        }
        {
            var Q0;
            Q0=makeQuery(id+"F1.opExtrude","CAP_EDGE",EDGE,{"disambiguationData":[OSD([sQuery(id+"F0.wireOp",EDGE,"E2.top")])],"isStart":false});
            var Q1;
            Q1=makeQuery(id+"F3.boolean.opBoolean","COPY",EDGE,{"derivedFrom":makeQuery(id+"F3.opExtrude","CAP_EDGE",EDGE,{"disambiguationData":[OSD([sQuery(id+"F2.wireOp",EDGE,"E8")])],"isStart":true})});
            fillet(context, id + "F37", {"entities" : qUnion([Q0, Q1]), "radius" : 1 * mm, "tangentPropagation" : true, "allowEdgeOverflow" : false});
        }
    });
